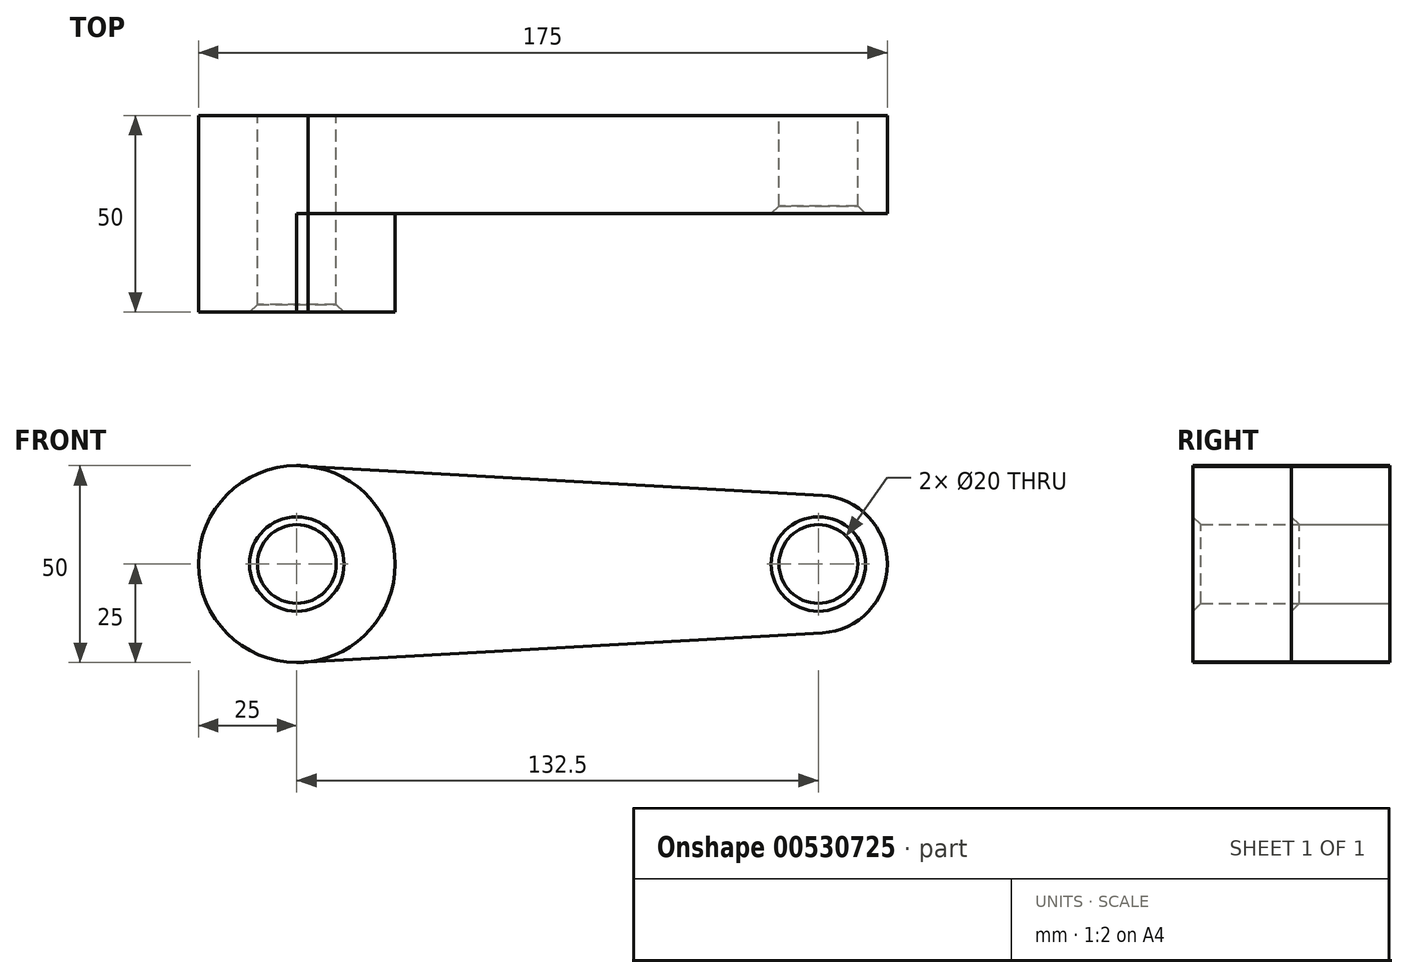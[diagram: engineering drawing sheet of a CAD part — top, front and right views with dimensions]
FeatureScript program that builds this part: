
annotation { "Feature Type Name" : "Feature", "Feature Type Description" : "" }
export const myFeature = defineFeature(function(context is Context, id is Id, definition is map)
    precondition{}
    {
        {
            var Q0;
            Q0=qCreatedBy(makeId("Front.planeOp"),FACE);
            var sketch = newSketch(context, id + "F0", { "sketchPlane" : qUnion([Q0])});
            skCircle(sketch, "E0", {"center": v(0, 0) * mm, "radius": 25 * mm});
            skCircle(sketch, "E1", {"center": v(132.5, 0) * mm, "radius": 17.5 * mm});
            skLineSegment(sketch, "E2", {"start": v(0, 25) * mm, "end": v(133.49, 17.47) * mm});
            skCircle(sketch, "E3", {"center": v(0, 0) * mm, "radius": 10 * mm});
            skCircle(sketch, "E4", {"center": v(132.5, 0) * mm, "radius": 10 * mm});
            skLineSegment(sketch, "E5", {"start": v(0, -25) * mm, "end": v(133.49, -17.47) * mm});
            skSolve(sketch);
        }
        {
            var Q0;
            Q0 = qSketchRegion(id + "F0", true);
            extrude(context, id + "F1", {"entities" : qUnion([Q0]), "depth" : 25 * mm, "offsetDistance" : 25 * mm});
        }
        {
            var Q0;
            Q0=makeQuery(id+"F0.imprint","IMPRINT",FACE,{"disambiguationData":[TD([[makeQuery(id+"F0.imprint","IMPRINT",EDGE,{"derivedFrom":sQuery(id+"F0.wireOp",EDGE,"E3")}),-1.0]])]});
            extrude(context, id + "F2", {"entities" : qUnion([Q0]), "operationType" : NewBodyOperationType.ADD, "depth" : 50 * mm, "offsetDistance" : 25 * mm});
        }
        {
            var Q0;
            Q0=makeQuery(id+"F2.opExtrude","CAP_EDGE",EDGE,{"disambiguationData":[OSD([sQuery(id+"F0.wireOp",EDGE,"E3")])],"isStart":false});
            var Q1;
            {var subQ0=sQuery(id+"F0.wireOp",EDGE,"E0");Q1=makeQuery(id+"F2.opExtrude","CAP_EDGE",EDGE,{"disambiguationData":[OSD([subQ0]),TDD([makeQuery(id+"F0.imprint","IMPRINT",EDGE,{"disambiguationData":[TD([[makeQuery(id+"F0.imprint","INTERSECT",VERTEX,{"disambiguationData":[OD(0.0)],"derivedFrom":[subQ0,sQuery(id+"F0.wireOp",EDGE,"E2")]}),-1.0]])],"derivedFrom":subQ0})])],"isStart":false});}
            var Q2;
            Q2=makeQuery(id+"F1.opExtrude","CAP_EDGE",EDGE,{"disambiguationData":[OSD([sQuery(id+"F0.wireOp",EDGE,"E4")])],"isStart":false});
            chamfer(context, id + "F3", {"entities" : qUnion([Q0, Q1, Q2]), "width" : 2 * mm, "tangentPropagation" : true});
        }
    });
